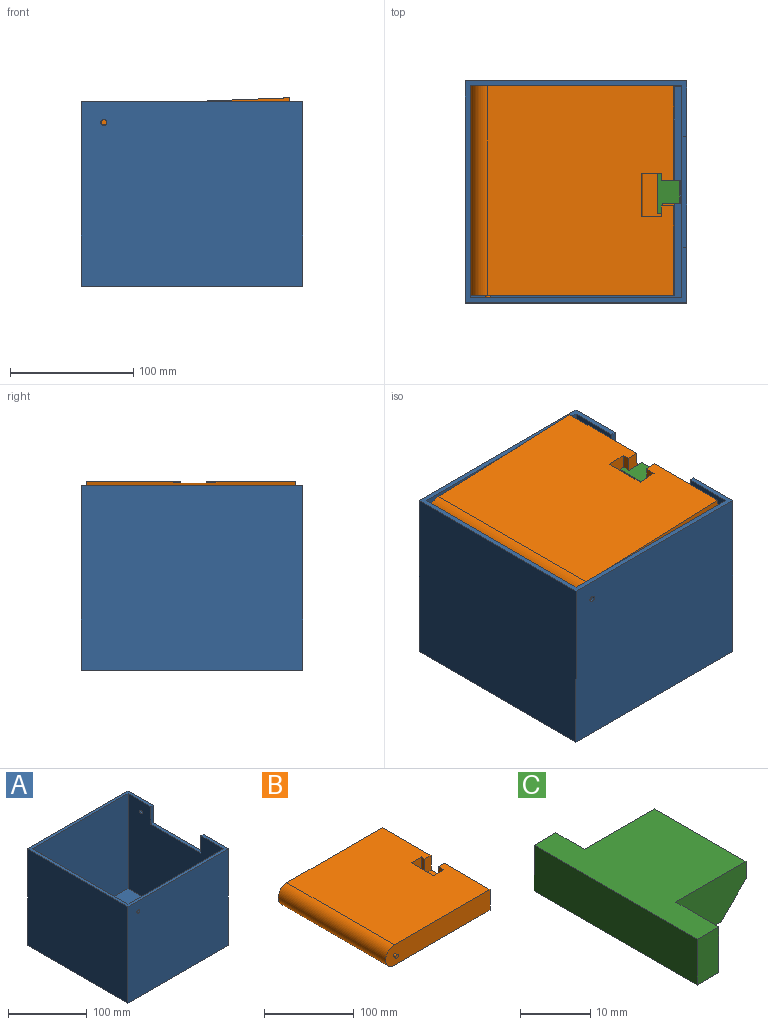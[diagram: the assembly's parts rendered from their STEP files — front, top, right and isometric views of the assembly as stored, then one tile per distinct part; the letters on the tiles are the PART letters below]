
ASSEMBLY  parts=3 mates=2
PART A: 18 faces, bbox 180x180x150 mm
  f0: plane 180x150mm, normal (1,0,0), area 24528.4mm2, adj f1,f4,f5,f6,f13,f14,f15,f16
  f1: plane 180x180mm, normal (0,0,1), area 2456mm2, adj f0,f2,f3,f4,f5,f7,f8,f9
  f2: plane 172x148mm, normal (-1,0,0), area 22984.4mm2, adj f1,f8,f9,f10,f13,f14,f15,f16
  f3: plane 180x150mm, normal (-1,0,0), area 27000mm2, adj f1,f4,f5,f6
  f4: plane 180x150mm, normal (0,-1,0), area 26980.4mm2, adj f0,f1,f3,f6,f12
  f5: plane 180x150mm, normal (0,1,0), area 26980.4mm2, adj f0,f1,f3,f6,f11
  f6: plane 180x180mm, normal (0,0,-1), area 32400mm2, adj f0,f3,f4,f5
  f7: plane 172x148mm, normal (1,0,0), area 25456mm2, adj f1,f8,f9,f10
  f8: plane 172x148mm, normal (0,1,0), area 25436.4mm2, adj f1,f2,f7,f10,f12
  f9: plane 172x148mm, normal (0,-1,0), area 25436.4mm2, adj f1,f2,f7,f10,f11
  f10: plane 172x172mm, normal (0,0,1), area 29584mm2, adj f2,f7,f8,f9
  f11: cylinder r=2.5mm len=5mm, axis (0,1,0), area 62.8mm2, adj f5,f9
  f12: cylinder r=2.5mm len=5mm, axis (0,1,0), area 62.8mm2, adj f4,f8
  f13: plane 27.03x4mm, normal (0,1,0), area 108.1mm2, adj f0,f1,f2,f14
  f14: plane 90x4mm, normal (0,0,1), area 360mm2, adj f0,f2,f13,f15
  f15: plane 27.03x4mm, normal (0,-1,0), area 108.1mm2, adj f0,f1,f2,f14
  f16: cylinder r=2.5mm len=5mm, axis (1,0,0), area 62.8mm2, adj f0,f2
  f17: cylinder r=2.5mm len=5mm, axis (1,0,0), area 62.8mm2, adj f0,f2
PART B: 18 faces, bbox 165x177x28 mm
  f0: plane 170x28mm, normal (1,0,0), area 4347.2mm2, adj f1,f2,f3,f4,f11,f12,f17
  f1: plane 165x28mm, normal (0,-1,0), area 4522mm2, adj f0,f3,f4,f7,f9
  f2: plane 165x28mm, normal (0,1,0), area 4523.3mm2, adj f0,f3,f4,f5,f9
  f3: plane 170x151mm, normal (0,0,1), area 24905mm2, adj f0,f1,f2,f9,f10,f11,f12,f13
  f4: plane 170x151mm, normal (0,0,-1), area 25670mm2, adj f0,f1,f2,f9
  f5: cylinder r=2mm len=4mm, axis (0,-1,0), area 37.7mm2, adj f2,f6
  f6: plane 4x4mm, normal (0,1,0), area 12.6mm2, adj f5
  f7: cylinder r=2.1mm len=4.2mm, axis (0,1,0), area 52.8mm2, adj f1,f8
  f8: plane 4.2x4.2mm, normal (0,-1,0), area 13.9mm2, adj f7
  f9: cylinder r=14mm len=170mm, axis (0,1,0), area 7477mm2, adj f1,f2,f3,f4
  f10: plane 20x8.9mm, normal (-1,0,0), area 178.1mm2, adj f3,f11,f16,f17
  f11: plane 20x9.52mm, normal (0,1,0), area 190.5mm2, adj f0,f3,f10,f17
  f12: plane 20x9.52mm, normal (0,-1,0), area 190.5mm2, adj f0,f3,f13,f17
  f13: plane 20x5.83mm, normal (-1,0,0), area 116.7mm2, adj f3,f12,f14,f17
  f14: plane 20x16.07mm, normal (0,-1,0), area 321.3mm2, adj f3,f13,f15,f17
  f15: plane 35.38x20mm, normal (1,0,0), area 707.5mm2, adj f3,f14,f16,f17
  f16: plane 20x16.07mm, normal (0,1,0), area 321.3mm2, adj f3,f10,f15,f17
  f17: plane 35.38x25.59mm, normal (0,0,1), area 765mm2, adj f0,f10,f11,f12,f13,f14,f15,f16
PART C: 11 faces, bbox 18.6x32.9x8 mm
  f0: plane 14.17x8mm, normal (0,-1,0), area 100.8mm2, adj f1,f7,f8,f9,f10
  f1: plane 18.45x3mm, normal (1,0,0), area 55.3mm2, adj f0,f2,f8,f10
  f2: plane 14.17x8mm, normal (0,1,0), area 100.8mm2, adj f1,f3,f8,f9,f10
  f3: plane 8x5.82mm, normal (1,0,0), area 46.6mm2, adj f2,f4,f8,f9
  f4: plane 8x4.39mm, normal (0,1,0), area 35.1mm2, adj f3,f5,f8,f9
  f5: plane 32.95x8mm, normal (-1,0,0), area 263.6mm2, adj f4,f6,f8,f9
  f6: plane 8x4.39mm, normal (0,-1,0), area 35.1mm2, adj f5,f7,f8,f9
  f7: plane 8.68x8mm, normal (1,0,0), area 69.4mm2, adj f0,f6,f8,f9
  f8: plane 32.95x18.56mm, normal (0,0,1), area 406.1mm2, adj f0,f1,f2,f3,f4,f5,f6,f7
  f9: plane 32.95x13.56mm, normal (0,0,-1), area 313.9mm2, adj f0,f2,f3,f4,f5,f6,f7,f10
  f10: plane 18.45x5mm, normal (0.71,0,-0.71), area 130.5mm2, adj f0,f1,f2,f9
PLACE A t=(96.25,-68.95,-227.57)mm
PLACE B rot(axis=(0,-1,0),2.3deg) t=(98.44,-67.95,-224.76)mm
PLACE C rot(axis=(0,-1,0),2.3deg) t=(100.26,-67.11,-226.69)mm
MATE revolute B.f9 <-> A.f11  axis (0,1,0) through (24.75,17.05,-94.57)mm
MATE planar B.f17 <-> C.f9  axis (-0.04,0,1) through (161.61,-71.19,-95.17)mm
